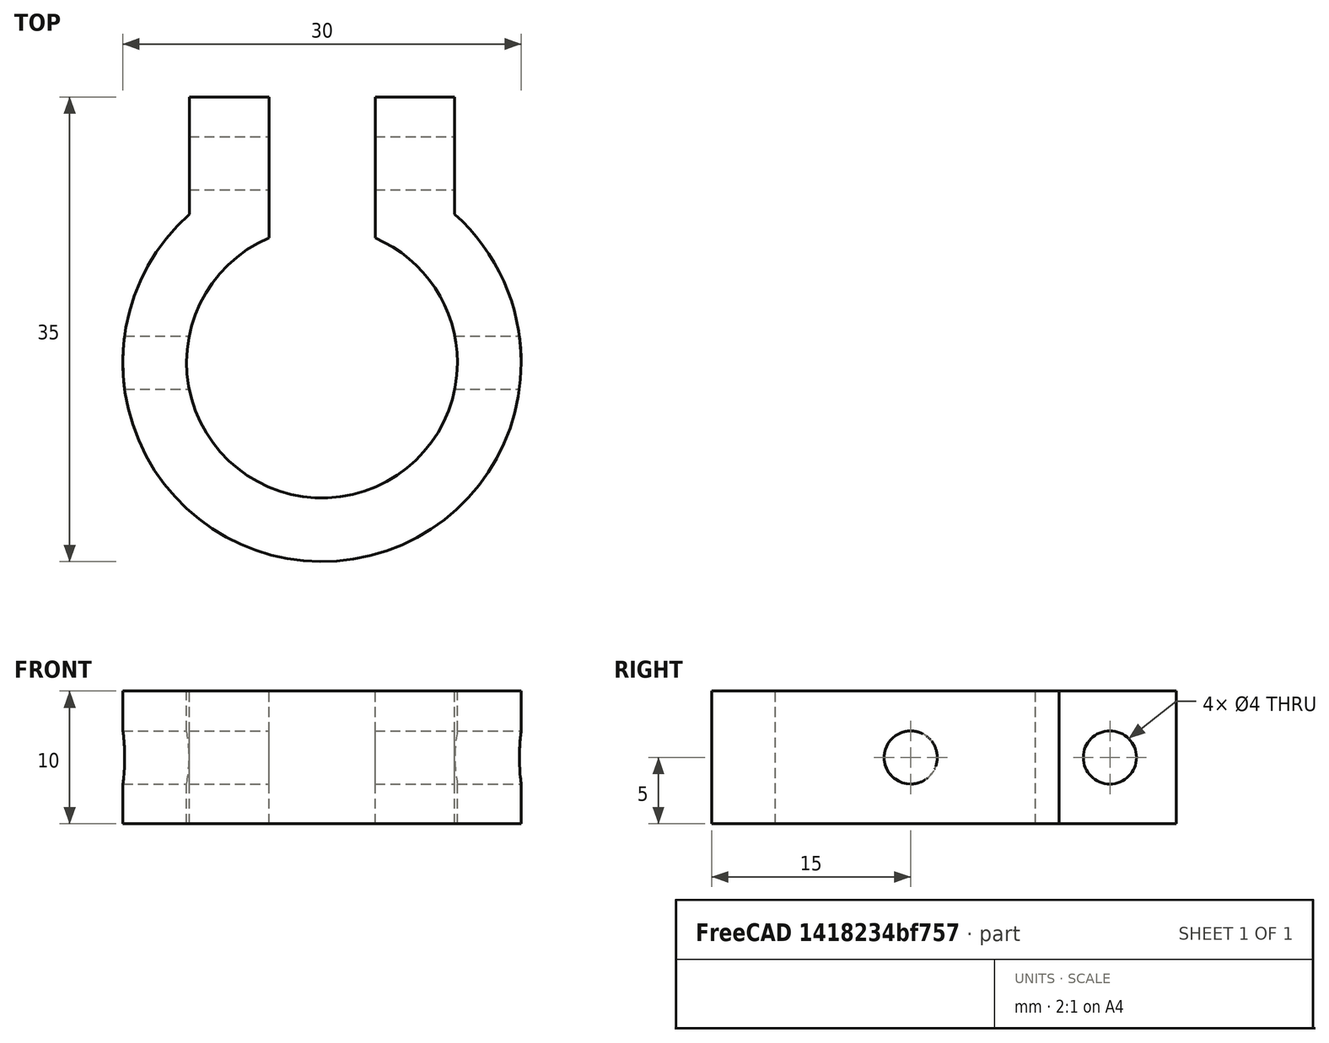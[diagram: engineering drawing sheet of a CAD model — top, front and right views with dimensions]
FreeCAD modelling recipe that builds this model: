
FCSTD DOCUMENT  (FreeCAD 0.18R16110 (Git))
Label: RackClip
License: All rights reserved
LicenseURL: http://en.wikipedia.org/wiki/All_rights_reserved
objects: Part::Cylinder×4, Part::Box×2, Part::MultiFuse×2, Part::Cut×1
note: 9 computed .brp shape members not serialized (recipe doc carries the construction recipe); baked Part::Feature solids carry a one-line shape summary decoded from their .brp

FEATURE [Part::Cylinder] Cylinder
  Angle = 360
  AttacherType = Attacher::AttachEngine3D
  Height = 10
  Radius = 15
FEATURE [Part::Cylinder] Cylinder001
  Angle = 360
  AttacherType = Attacher::AttachEngine3D
  Height = 10
  Radius = 10.2
FEATURE [Part::Box] Box  label="Cube"
  AttacherType = Attacher::AttachEngine3D
  Height = 10
  Length = 20
  Placement = pos=(-10,10,0) rot=(0,0,1;0rad)
  Width = 10
FEATURE [Part::MultiFuse] Fusion  label="Positive Fusion"
  Shapes = -> [Cylinder,Box]
FEATURE [Part::Cylinder] Cylinder002
  Angle = 360
  AttacherType = Attacher::AttachEngine3D
  Height = 40
  Placement = pos=(-20,0,5) rot=(0,1,0;1.5708rad)
  Radius = 2
FEATURE [Part::Cylinder] Cylinder003
  Angle = 360
  AttacherType = Attacher::AttachEngine3D
  Height = 40
  Placement = pos=(-20,15,5) rot=(0,1,0;1.5708rad)
  Radius = 2
FEATURE [Part::Box] Box001  label="Cube001"
  AttacherType = Attacher::AttachEngine3D
  Height = 10
  Length = 8
  Placement = pos=(-4,5,0) rot=(0,0,1;0rad)
  Width = 15
FEATURE [Part::MultiFuse] Fusion001  label="Negative Fusion"
  Shapes = -> [Box001,Cylinder003,Cylinder002,Cylinder001]
FEATURE [Part::Cut] Cut
  Base = -> Fusion
  Tool = -> Fusion001
